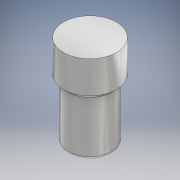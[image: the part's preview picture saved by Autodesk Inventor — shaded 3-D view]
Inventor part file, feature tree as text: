
AUTODESK INVENTOR PART (.ipt)
format: ipt  version: 2018.3 (Build 223284000, 284)  size: 118,784 bytes
history: native  units: mm
features: extrude x2, sketch x2, fillet x1, chamfer x1
ambient origin geometry x8: Origin, YZ Plane, XZ Plane, XY Plane, X Axis, Y Axis, Z Axis, Center Point
bodies: Solid1 (feature_tree)
feature tree (6):
  extrude  "Extrusion1"  Depth=37.0mm TaperAngle=0.0deg
  extrude  "Extrusion2"  Depth=2.0mm TaperAngle=0.0deg
  fillet  "Fillet1"  Radius=2.0mm
  chamfer  "Chamfer1"  Distance=2.0mm Angle=45.0deg
  sketch  "Sketch1"  dims[d0=27.0mm d1=37.0mm d2=0.0mm]
  sketch  "Sketch2"  dims[d3=33.0mm d4=20.0mm d5=0.0mm d6=2.0mm d7=3.0mm d8=2.0mm d9=45.0deg]
